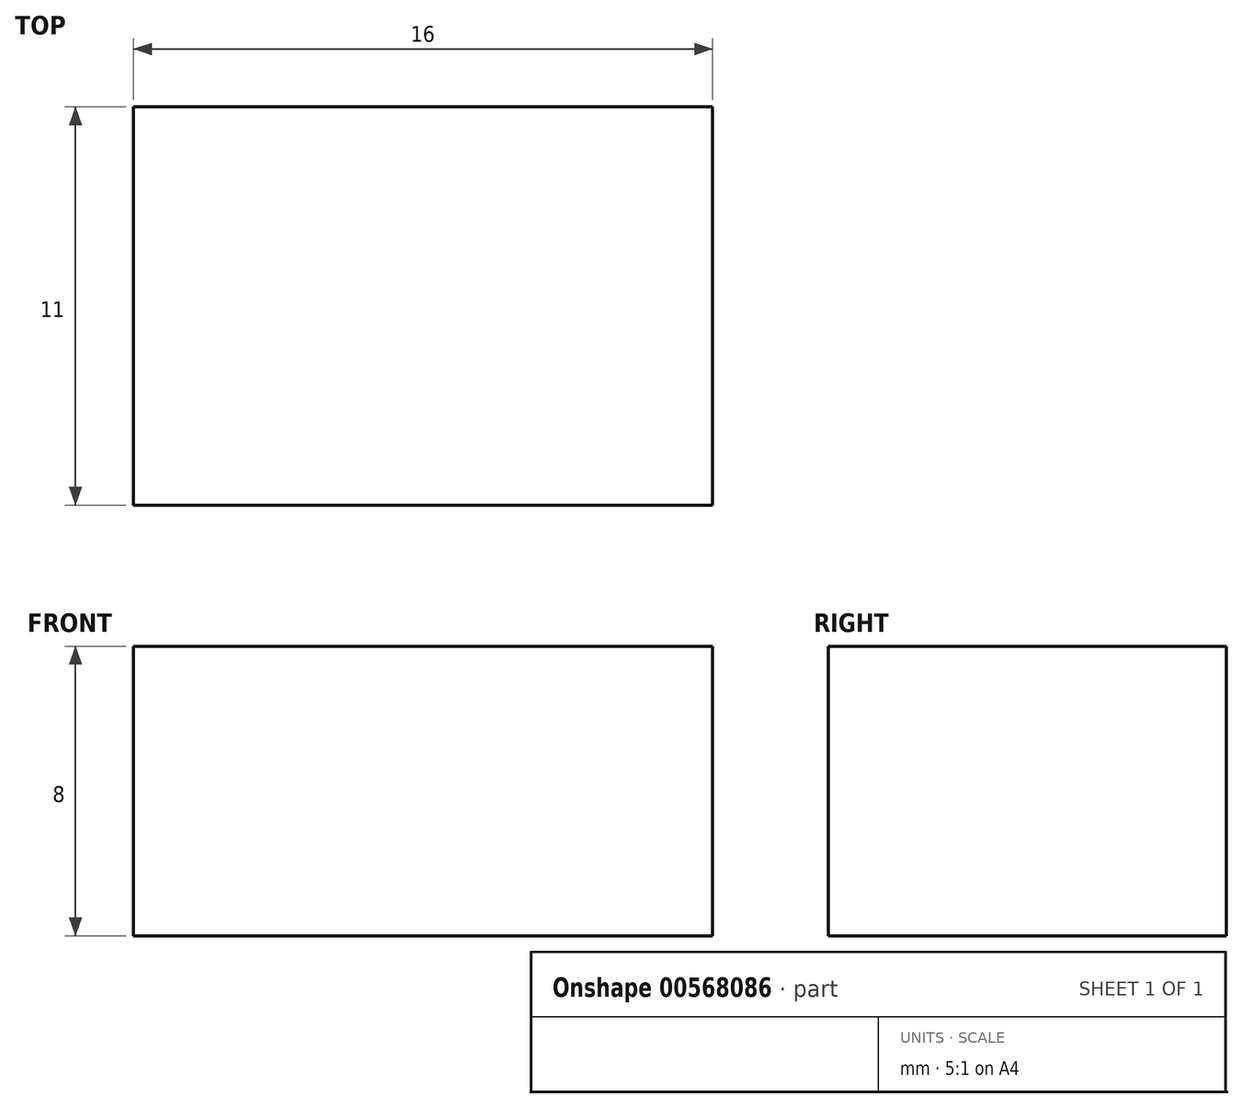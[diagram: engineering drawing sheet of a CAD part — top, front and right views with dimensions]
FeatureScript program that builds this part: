
annotation { "Feature Type Name" : "Feature", "Feature Type Description" : "" }
export const myFeature = defineFeature(function(context is Context, id is Id, definition is map)
    precondition{}
    {
        {
            var Q0;
            Q0=qCreatedBy(makeId("Top.planeOp"),FACE);
            var sketch = newSketch(context, id + "F0", { "sketchPlane" : qUnion([Q0])});
            skLineSegment(sketch, "E0.bottom", {"start": v(8, 5.5) * mm, "end": v(-8, 5.5) * mm});
            skLineSegment(sketch, "E0.top", {"start": v(8, -5.5) * mm, "end": v(-8, -5.5) * mm});
            skLineSegment(sketch, "E0.left", {"start": v(8, 5.5) * mm, "end": v(8, -5.5) * mm});
            skLineSegment(sketch, "E0.right", {"start": v(-8, 5.5) * mm, "end": v(-8, -5.5) * mm});
            skPoint(sketch, "E0.middle", {"position": v(0, 0) * mm});
            skSolve(sketch);
        }
        {
            var Q0;
            Q0 = qSketchRegion(id + "F0", true);
            extrude(context, id + "F1", {"entities" : qUnion([Q0]), "depth" : 8 * mm, "offsetDistance" : 25.4 * mm});
        }
    });
